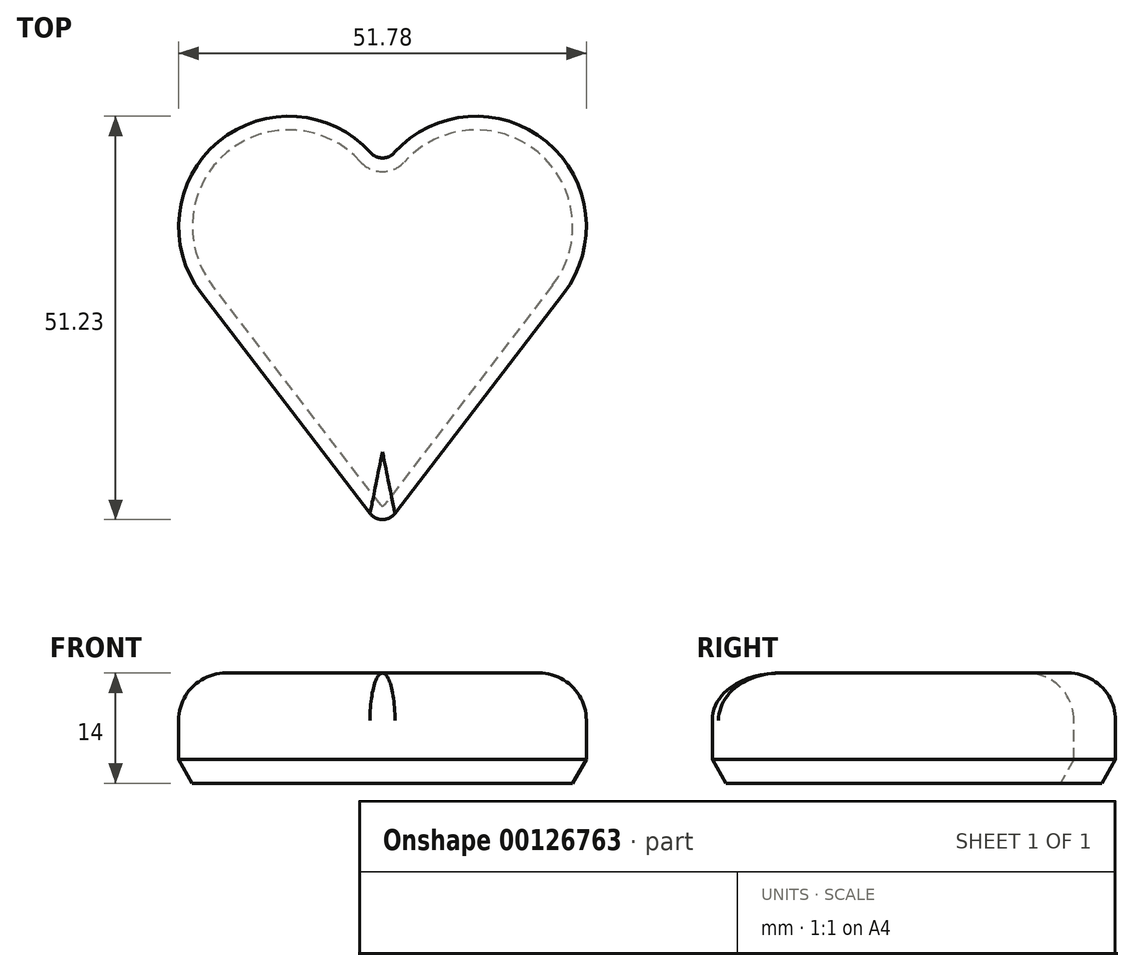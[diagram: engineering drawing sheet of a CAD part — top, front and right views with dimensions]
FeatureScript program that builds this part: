
annotation { "Feature Type Name" : "Feature", "Feature Type Description" : "" }
export const myFeature = defineFeature(function(context is Context, id is Id, definition is map)
    precondition{}
    {
        {
            var Q0;
            Q0=qCreatedBy(makeId("Top.planeOp"),FACE);
            var sketch = newSketch(context, id + "F0", { "sketchPlane" : qUnion([Q0])});
            skLineSegment(sketch, "E0", {"start": v(-23, 0) * mm, "end": v(0, -30) * mm});
            skLineSegment(sketch, "E1", {"start": v(0, -30) * mm, "end": v(23, 0) * mm});
            skArc(sketch, "E2", {"start": v(23, 0) * mm, "mid": v(19.85, 20.03) * mm, "end": v(0, 15.9) * mm});
            skArc(sketch, "E3", {"start": v(-23, 0) * mm, "mid": v(-19.85, 20.03) * mm, "end": v(0, 15.9) * mm});
            skSolve(sketch);
        }
        {
            var Q0;
            Q0=qSketchRegion(id+"F0",true);
            extrude(context, id + "F1", {"entities" : qUnion([Q0]), "depth" : 14 * mm});
        }
        {
            var Q0;
            Q0=makeQuery(id+"F1.opExtrude","SWEPT_EDGE",EDGE,{"disambiguationData":[OSD([sQuery(id+"F0.wireOp",EDGE,"E0"),sQuery(id+"F0.wireOp",EDGE,"E1")])]});
            var Q1;
            Q1=makeQuery(id+"F1.opExtrude","SWEPT_EDGE",EDGE,{"disambiguationData":[OSD([sQuery(id+"F0.wireOp",EDGE,"E2"),sQuery(id+"F0.wireOp",EDGE,"E3")])]});
            fillet(context, id + "F2", {"entities" : qUnion([Q0, Q1]), "radius" : 2 * mm, "tangentPropagation" : true, "allowEdgeOverflow" : false});
        }
        {
            var Q0;
            Q0=makeQuery(id+"F1.opExtrude","CAP_EDGE",EDGE,{"disambiguationData":[OSD([sQuery(id+"F0.wireOp",EDGE,"E1")])],"isStart":false});
            fillet(context, id + "F3", {"entities" : qUnion([Q0]), "radius" : 6 * mm, "tangentPropagation" : true, "allowEdgeOverflow" : false});
        }
        {
            var Q0;
            Q0=makeQuery(id+"F1.opExtrude","CAP_EDGE",EDGE,{"disambiguationData":[OSD([sQuery(id+"F0.wireOp",EDGE,"E0")])],"isStart":true});
            chamfer(context, id + "F4", {"entities" : qUnion([Q0]), "chamferType" : ChamferType.OFFSET_ANGLE, "width" : 3 * mm, "oppositeDirection" : false, "angle" : 30 * degree, "tangentPropagation" : true});
        }
    });
